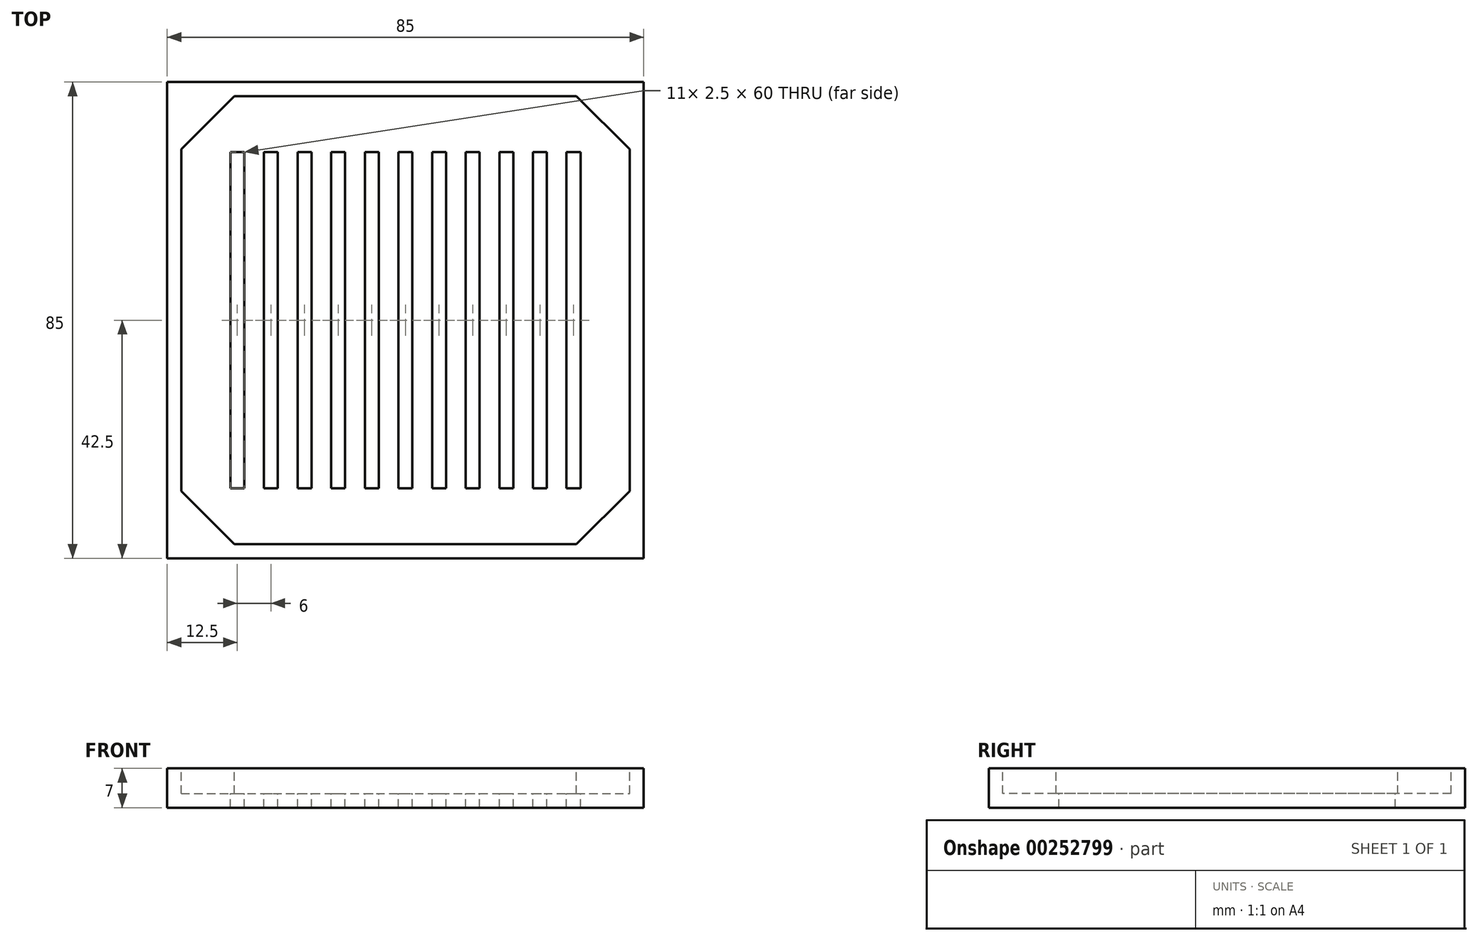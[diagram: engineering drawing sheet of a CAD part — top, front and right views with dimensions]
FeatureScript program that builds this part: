
annotation { "Feature Type Name" : "Feature", "Feature Type Description" : "" }
export const myFeature = defineFeature(function(context is Context, id is Id, definition is map)
    precondition{}
    {
        {
            var Q0;
            Q0=qCreatedBy(makeId("Top.planeOp"),FACE);
            var sketch = newSketch(context, id + "F0", { "sketchPlane" : qUnion([Q0])});
            skLineSegment(sketch, "E0.bottom", {"start": v(-42.5, 42.5) * mm, "end": v(42.5, 42.5) * mm});
            skLineSegment(sketch, "E0.top", {"start": v(-42.5, -42.5) * mm, "end": v(42.5, -42.5) * mm});
            skLineSegment(sketch, "E0.left", {"start": v(-42.5, 42.5) * mm, "end": v(-42.5, -42.5) * mm});
            skLineSegment(sketch, "E0.right", {"start": v(42.5, 42.5) * mm, "end": v(42.5, -42.5) * mm});
            skSolve(sketch);
        }
        {
            var Q0;
            Q0 = qSketchRegion(id + "F0", true);
            extrude(context, id + "F1", {"entities" : qUnion([Q0]), "depth" : 7 * mm});
        }
        {
            var Q0;
            Q0=makeQuery(id+"F1.opExtrude","CAP_FACE",FACE,{"disambiguationData":[OSD([sQuery(id+"F0.wireOp",EDGE,"E0.bottom"),sQuery(id+"F0.wireOp",EDGE,"E0.top"),sQuery(id+"F0.wireOp",EDGE,"E0.left"),sQuery(id+"F0.wireOp",EDGE,"E0.right")])],"isStart":false});
            var sketch = newSketch(context, id + "F2", { "sketchPlane" : qUnion([Q0])});
            skLineSegment(sketch, "E1.bottom", {"start": v(-30.5, 40) * mm, "end": v(30.5, 40) * mm});
            skLineSegment(sketch, "E1.top", {"start": v(-30.5, -40) * mm, "end": v(30.5, -40) * mm});
            skLineSegment(sketch, "E1.left", {"start": v(-40, 30.5) * mm, "end": v(-40, -30.5) * mm});
            skLineSegment(sketch, "E1.right", {"start": v(40, 30.5) * mm, "end": v(40, -30.5) * mm});
            skLineSegment(sketch, "E2", {"start": v(-40, 30.5) * mm, "end": v(-30.5, 40) * mm});
            skLineSegment(sketch, "E3", {"start": v(30.5, 40) * mm, "end": v(40, 30.5) * mm});
            skLineSegment(sketch, "E4", {"start": v(40, -30.5) * mm, "end": v(30.5, -40) * mm});
            skLineSegment(sketch, "E5", {"start": v(-40, -30.5) * mm, "end": v(-30.5, -40) * mm});
            skPoint(sketch, "E6.orphan", {"position": v(-40, 40) * mm});
            skPoint(sketch, "E7.orphan", {"position": v(40, 40) * mm});
            skPoint(sketch, "E8.orphan", {"position": v(40, -40) * mm});
            skPoint(sketch, "E9.orphan", {"position": v(-40, -40) * mm});
            skSolve(sketch);
        }
        {
            var Q0;
            Q0=makeQuery(id+"F2.imprint","IMPRINT",FACE,{"disambiguationData":[TD([[makeQuery(id+"F2.imprint","IMPRINT",EDGE,{"derivedFrom":sQuery(id+"F2.wireOp",EDGE,"E1.bottom")}),-1.0]])]});
            extrude(context, id + "F3", {"entities" : qUnion([Q0]), "operationType" : NewBodyOperationType.REMOVE, "oppositeDirection" : true, "depth" : 4.5 * mm});
        }
        {
            var Q0;
            Q0=makeQuery(id+"F2.imprint","IMPRINT",FACE,{"disambiguationData":[TD([[makeQuery(id+"F2.imprint","IMPRINT",EDGE,{"derivedFrom":sQuery(id+"F2.wireOp",EDGE,"E1.bottom")}),-1.0]])]});
            var sketch = newSketch(context, id + "F4", { "sketchPlane" : qUnion([Q0])});
            skLineSegment(sketch, "E10.bottom", {"start": v(-31.25, 30) * mm, "end": v(-28.75, 30) * mm});
            skLineSegment(sketch, "E10.top", {"start": v(-31.25, -30) * mm, "end": v(-28.75, -30) * mm});
            skLineSegment(sketch, "E10.left", {"start": v(-31.25, 30) * mm, "end": v(-31.25, -30) * mm});
            skLineSegment(sketch, "E10.right", {"start": v(-28.75, 30) * mm, "end": v(-28.75, -30) * mm});
            skLineSegment(sketch, "E11.1.0.0", {"start": v(-25.25, 30) * mm, "end": v(-25.25, -30) * mm});
            skLineSegment(sketch, "E11.1.0.1", {"start": v(-25.25, 30) * mm, "end": v(-22.75, 30) * mm});
            skLineSegment(sketch, "E11.1.0.2", {"start": v(-22.75, 30) * mm, "end": v(-22.75, -30) * mm});
            skLineSegment(sketch, "E11.1.0.3", {"start": v(-25.25, -30) * mm, "end": v(-22.75, -30) * mm});
            skLineSegment(sketch, "E11.2.0.0", {"start": v(-19.25, 30) * mm, "end": v(-19.25, -30) * mm});
            skLineSegment(sketch, "E11.2.0.1", {"start": v(-19.25, 30) * mm, "end": v(-16.75, 30) * mm});
            skLineSegment(sketch, "E11.2.0.2", {"start": v(-16.75, 30) * mm, "end": v(-16.75, -30) * mm});
            skLineSegment(sketch, "E11.2.0.3", {"start": v(-19.25, -30) * mm, "end": v(-16.75, -30) * mm});
            skLineSegment(sketch, "E11.direction1", {"start": v(-31.25, -30) * mm, "end": v(-25.25, -30) * mm, "construction": true});
            skLineSegment(sketch, "E12.0.3.0", {"start": v(-13.25, 30) * mm, "end": v(-13.25, -30) * mm});
            skLineSegment(sketch, "E12.3.3.0", {"start": v(-13.25, 30) * mm, "end": v(-10.75, 30) * mm});
            skLineSegment(sketch, "E12.6.3.0", {"start": v(-10.75, 30) * mm, "end": v(-10.75, -30) * mm});
            skLineSegment(sketch, "E12.9.3.0", {"start": v(-13.25, -30) * mm, "end": v(-10.75, -30) * mm});
            skLineSegment(sketch, "E12.0.4.0", {"start": v(-7.25, 30) * mm, "end": v(-7.25, -30) * mm});
            skLineSegment(sketch, "E12.3.4.0", {"start": v(-7.25, 30) * mm, "end": v(-4.75, 30) * mm});
            skLineSegment(sketch, "E12.6.4.0", {"start": v(-4.75, 30) * mm, "end": v(-4.75, -30) * mm});
            skLineSegment(sketch, "E12.9.4.0", {"start": v(-7.25, -30) * mm, "end": v(-4.75, -30) * mm});
            skLineSegment(sketch, "E12.0.5.0", {"start": v(-1.25, 30) * mm, "end": v(-1.25, -30) * mm});
            skLineSegment(sketch, "E12.3.5.0", {"start": v(-1.25, 30) * mm, "end": v(1.25, 30) * mm});
            skLineSegment(sketch, "E12.6.5.0", {"start": v(1.25, 30) * mm, "end": v(1.25, -30) * mm});
            skLineSegment(sketch, "E12.9.5.0", {"start": v(-1.25, -30) * mm, "end": v(1.25, -30) * mm});
            skLineSegment(sketch, "E12.0.6.0", {"start": v(4.75, 30) * mm, "end": v(4.75, -30) * mm});
            skLineSegment(sketch, "E12.3.6.0", {"start": v(4.75, 30) * mm, "end": v(7.25, 30) * mm});
            skLineSegment(sketch, "E12.6.6.0", {"start": v(7.25, 30) * mm, "end": v(7.25, -30) * mm});
            skLineSegment(sketch, "E12.9.6.0", {"start": v(4.75, -30) * mm, "end": v(7.25, -30) * mm});
            skLineSegment(sketch, "E12.0.7.0", {"start": v(10.75, 30) * mm, "end": v(10.75, -30) * mm});
            skLineSegment(sketch, "E12.3.7.0", {"start": v(10.75, 30) * mm, "end": v(13.25, 30) * mm});
            skLineSegment(sketch, "E12.6.7.0", {"start": v(13.25, 30) * mm, "end": v(13.25, -30) * mm});
            skLineSegment(sketch, "E12.9.7.0", {"start": v(10.75, -30) * mm, "end": v(13.25, -30) * mm});
            skLineSegment(sketch, "E12.0.8.0", {"start": v(16.75, 30) * mm, "end": v(16.75, -30) * mm});
            skLineSegment(sketch, "E12.3.8.0", {"start": v(16.75, 30) * mm, "end": v(19.25, 30) * mm});
            skLineSegment(sketch, "E12.6.8.0", {"start": v(19.25, 30) * mm, "end": v(19.25, -30) * mm});
            skLineSegment(sketch, "E12.9.8.0", {"start": v(16.75, -30) * mm, "end": v(19.25, -30) * mm});
            skLineSegment(sketch, "E12.0.9.0", {"start": v(22.75, 30) * mm, "end": v(22.75, -30) * mm});
            skLineSegment(sketch, "E12.3.9.0", {"start": v(22.75, 30) * mm, "end": v(25.25, 30) * mm});
            skLineSegment(sketch, "E12.6.9.0", {"start": v(25.25, 30) * mm, "end": v(25.25, -30) * mm});
            skLineSegment(sketch, "E12.9.9.0", {"start": v(22.75, -30) * mm, "end": v(25.25, -30) * mm});
            skLineSegment(sketch, "E12.0.10.0", {"start": v(28.75, 30) * mm, "end": v(28.75, -30) * mm});
            skLineSegment(sketch, "E12.3.10.0", {"start": v(28.75, 30) * mm, "end": v(31.25, 30) * mm});
            skLineSegment(sketch, "E12.6.10.0", {"start": v(31.25, 30) * mm, "end": v(31.25, -30) * mm});
            skLineSegment(sketch, "E12.9.10.0", {"start": v(28.75, -30) * mm, "end": v(31.25, -30) * mm});
            skSolve(sketch);
        }
        {
            var Q0;
            Q0 = qSketchRegion(id + "F4", true);
            extrude(context, id + "F5", {"entities" : qUnion([Q0]), "operationType" : NewBodyOperationType.REMOVE, "oppositeDirection" : true, "depth" : 25 * mm});
        }
    });
